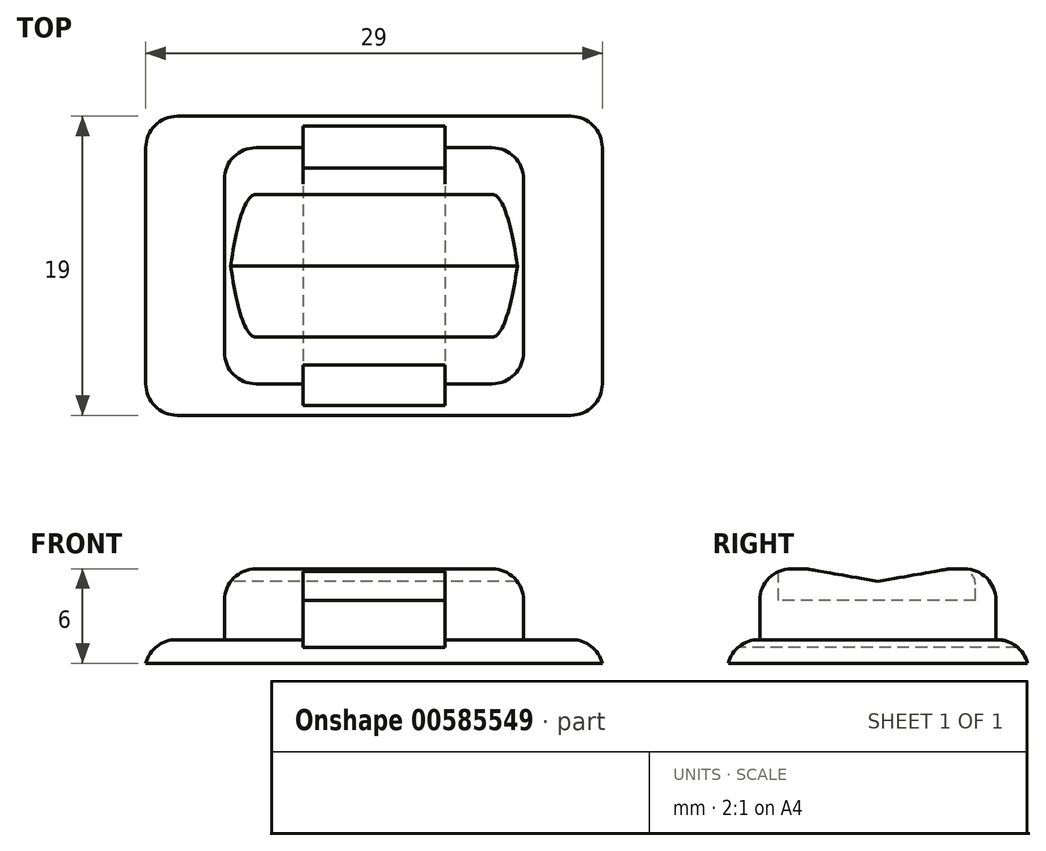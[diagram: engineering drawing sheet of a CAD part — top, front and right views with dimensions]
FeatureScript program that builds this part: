
annotation { "Feature Type Name" : "Feature", "Feature Type Description" : "" }
export const myFeature = defineFeature(function(context is Context, id is Id, definition is map)
    precondition{}
    {
        {
            var Q0;
            Q0=qCreatedBy(makeId("Top.planeOp"),FACE);
            var sketch = newSketch(context, id + "F0", { "sketchPlane" : qUnion([Q0])});
            skLineSegment(sketch, "E0.bottom", {"start": v(-12.5, 9.5) * mm, "end": v(12.5, 9.5) * mm});
            skLineSegment(sketch, "E0.top", {"start": v(-12.5, -9.5) * mm, "end": v(12.5, -9.5) * mm});
            skLineSegment(sketch, "E0.left", {"start": v(-14.5, 7.5) * mm, "end": v(-14.5, -7.5) * mm});
            skLineSegment(sketch, "E0.right", {"start": v(14.5, 7.5) * mm, "end": v(14.5, -7.5) * mm});
            skLineSegment(sketch, "E1", {"start": v(14.5, 9.5) * mm, "end": v(-14.5, -9.5) * mm, "construction": true});
            skLineSegment(sketch, "E2", {"start": v(-14.5, 9.5) * mm, "end": v(14.5, -9.5) * mm, "construction": true});
            skPoint(sketch, "E3.visualSharp", {"position": v(14.5, 9.5) * mm});
            skArc(sketch, "E3.filletArc", {"start": v(14.5, 7.5) * mm, "mid": v(13.91, 8.91) * mm, "end": v(12.5, 9.5) * mm});
            skPoint(sketch, "E4.visualSharp", {"position": v(-14.5, 9.5) * mm});
            skArc(sketch, "E4.filletArc", {"start": v(-12.5, 9.5) * mm, "mid": v(-13.91, 8.91) * mm, "end": v(-14.5, 7.5) * mm});
            skPoint(sketch, "E5.visualSharp", {"position": v(-14.5, -9.5) * mm});
            skArc(sketch, "E5.filletArc", {"start": v(-14.5, -7.5) * mm, "mid": v(-13.91, -8.91) * mm, "end": v(-12.5, -9.5) * mm});
            skPoint(sketch, "E6.visualSharp", {"position": v(14.5, -9.5) * mm});
            skArc(sketch, "E6.filletArc", {"start": v(12.5, -9.5) * mm, "mid": v(13.91, -8.91) * mm, "end": v(14.5, -7.5) * mm});
            skSolve(sketch);
        }
        {
            var Q0;
            Q0 = qSketchRegion(id + "F0", true);
            extrude(context, id + "F1", {"entities" : qUnion([Q0]), "depth" : 1.5 * mm, "offsetDistance" : 25 * mm});
        }
        {
            var Q0;
            Q0=makeQuery(id+"F1.opExtrude","CAP_FACE",FACE,{"disambiguationData":[OSD([sQuery(id+"F0.wireOp",EDGE,"E0.bottom"),sQuery(id+"F0.wireOp",EDGE,"E0.top"),sQuery(id+"F0.wireOp",EDGE,"E0.left"),sQuery(id+"F0.wireOp",EDGE,"E0.right")])],"isStart":false});
            var sketch = newSketch(context, id + "F2", { "sketchPlane" : qUnion([Q0])});
            skLineSegment(sketch, "E7.bottom", {"start": v(-9.5, 7.5) * mm, "end": v(9.5, 7.5) * mm});
            skLineSegment(sketch, "E7.top", {"start": v(-9.5, -7.5) * mm, "end": v(9.5, -7.5) * mm});
            skLineSegment(sketch, "E7.left", {"start": v(-9.5, 7.5) * mm, "end": v(-9.5, -7.5) * mm});
            skLineSegment(sketch, "E7.right", {"start": v(9.5, 7.5) * mm, "end": v(9.5, -7.5) * mm});
            skLineSegment(sketch, "E8", {"start": v(9.5, 7.5) * mm, "end": v(-9.5, -7.5) * mm, "construction": true});
            skLineSegment(sketch, "E9", {"start": v(-9.5, 7.5) * mm, "end": v(9.5, -7.5) * mm, "construction": true});
            skSolve(sketch);
        }
        {
            var Q0;
            Q0 = qSketchRegion(id + "F2", true);
            extrude(context, id + "F3", {"entities" : qUnion([Q0]), "operationType" : NewBodyOperationType.ADD, "depth" : 4.5 * mm, "offsetDistance" : 25 * mm});
        }
        {
            var Q0;
            Q0=qCreatedBy(makeId("Front.planeOp"),FACE);
            var sketch = newSketch(context, id + "F4", { "sketchPlane" : qUnion([Q0])});
            skLineSegment(sketch, "E10.bottom", {"start": v(-4.5, 4) * mm, "end": v(4.5, 4) * mm});
            skLineSegment(sketch, "E10.top", {"start": v(-4.5, 1) * mm, "end": v(4.5, 1) * mm});
            skLineSegment(sketch, "E10.left", {"start": v(-4.5, 4) * mm, "end": v(-4.5, 1) * mm});
            skLineSegment(sketch, "E10.right", {"start": v(4.5, 4) * mm, "end": v(4.5, 1) * mm});
            skLineSegment(sketch, "E11", {"start": v(4.5, 4) * mm, "end": v(-4.5, 1) * mm, "construction": true});
            skLineSegment(sketch, "E12", {"start": v(-4.5, 4) * mm, "end": v(4.5, 1) * mm, "construction": true});
            skPoint(sketch, "E13", {"position": v(0, 2.5) * mm});
            skSolve(sketch);
        }
        {
            var Q0;
            Q0 = qSketchRegion(id + "F4", true);
            extrude(context, id + "F5", {"entities" : qUnion([Q0]), "operationType" : NewBodyOperationType.REMOVE, "endBound" : BoundingType.SYMMETRIC, "oppositeDirection" : true, "depth" : 25 * mm, "offsetDistance" : 25 * mm});
        }
        {
            var Q0;
            Q0=makeQuery(id+"F3.opExtrude","SWEPT_FACE",FACE,{"disambiguationData":[OSD([sQuery(id+"F2.wireOp",EDGE,"E7.top")])]});
            var sketch = newSketch(context, id + "F6", { "sketchPlane" : qUnion([Q0])});
            skLineSegment(sketch, "E14.bottom", {"start": v(-4.5, 4) * mm, "end": v(4.5, 4) * mm});
            skLineSegment(sketch, "E14.top", {"start": v(-4.5, 6) * mm, "end": v(4.5, 6) * mm});
            skLineSegment(sketch, "E14.left", {"start": v(-4.5, 4) * mm, "end": v(-4.5, 6) * mm});
            skLineSegment(sketch, "E14.right", {"start": v(4.5, 4) * mm, "end": v(4.5, 6) * mm});
            skSolve(sketch);
        }
        {
            var Q0;
            Q0 = qSketchRegion(id + "F6", true);
            extrude(context, id + "F7", {"entities" : qUnion([Q0]), "operationType" : NewBodyOperationType.REMOVE, "oppositeDirection" : true, "depth" : 1.2 * mm, "offsetDistance" : 25 * mm});
        }
        {
            var Q0;
            Q0=makeQuery(id+"F3.opExtrude","SWEPT_FACE",FACE,{"disambiguationData":[OSD([sQuery(id+"F2.wireOp",EDGE,"E7.bottom")])]});
            var sketch = newSketch(context, id + "F8", { "sketchPlane" : qUnion([Q0])});
            skLineSegment(sketch, "E15.bottom", {"start": v(-4.5, 4) * mm, "end": v(4.5, 4) * mm});
            skLineSegment(sketch, "E15.top", {"start": v(-4.5, 6) * mm, "end": v(4.5, 6) * mm});
            skLineSegment(sketch, "E15.left", {"start": v(-4.5, 4) * mm, "end": v(-4.5, 6) * mm});
            skLineSegment(sketch, "E15.right", {"start": v(4.5, 4) * mm, "end": v(4.5, 6) * mm});
            skSolve(sketch);
        }
        {
            var Q0;
            Q0 = qSketchRegion(id + "F8", true);
            extrude(context, id + "F9", {"entities" : qUnion([Q0]), "operationType" : NewBodyOperationType.REMOVE, "oppositeDirection" : true, "depth" : 1.3 * mm, "offsetDistance" : 25 * mm});
        }
        {
            var Q0;
            Q0=makeQuery(id+"F3.opExtrude","CAP_EDGE",EDGE,{"disambiguationData":[OSD([sQuery(id+"F2.wireOp",EDGE,"E7.right")])],"isStart":false});
            var Q1;
            Q1=makeQuery(id+"F3.opExtrude","CAP_EDGE",EDGE,{"disambiguationData":[OSD([sQuery(id+"F2.wireOp",EDGE,"E7.left")])],"isStart":false});
            fillet(context, id + "F10", {"entities" : qUnion([Q0, Q1]), "radius" : 2 * mm, "tangentPropagation" : true, "allowEdgeOverflow" : false});
        }
        {
            var Q0;
            {var subQ0=sQuery(id+"F2.wireOp",EDGE,"E7.right");var subQ1=sQuery(id+"F2.wireOp",EDGE,"E7.bottom");Q0=makeQuery(id+"F10.opFillet","BLEND_EDGE",EDGE,{"blendedFrom":[makeQuery(id+"F3.opExtrude","CAP_EDGE",EDGE,{"disambiguationData":[OSD([subQ0])],"isStart":false}),makeQuery(id+"F9.boolean.opBoolean","SPLIT",FACE,{"disambiguationData":[TD([makeQuery(id+"F3.opExtrude","SWEPT_FACE",FACE,{"disambiguationData":[OSD([subQ0])]})])],"derivedFrom":makeQuery(id+"F3.opExtrude","SWEPT_FACE",FACE,{"disambiguationData":[OSD([subQ1])]})})],"blendedInto":[makeQuery(id+"F9.boolean.opBoolean","SPLIT",FACE,{"disambiguationData":[TD([makeQuery(id+"F3.opExtrude","SWEPT_FACE",FACE,{"disambiguationData":[OSD([subQ0])]})])],"derivedFrom":makeQuery(id+"F3.opExtrude","SWEPT_FACE",FACE,{"disambiguationData":[OSD([subQ1])]})})]});}
            var Q1;
            {var subQ0=sQuery(id+"F2.wireOp",EDGE,"E7.right");var subQ1=sQuery(id+"F2.wireOp",EDGE,"E7.bottom");Q1=makeQuery(id+"F9.boolean.opBoolean","SPLIT",EDGE,{"disambiguationData":[TD([makeQuery(id+"F3.opExtrude","SWEPT_FACE",FACE,{"disambiguationData":[OSD([subQ0])]})])],"derivedFrom":makeQuery(id+"F3.opExtrude","CAP_EDGE",EDGE,{"disambiguationData":[OSD([subQ1])],"isStart":false})});}
            var Q2;
            Q2=makeQuery(id+"F3.opExtrude","SWEPT_EDGE",EDGE,{"disambiguationData":[OSD([sQuery(id+"F2.wireOp",EDGE,"E7.bottom"),sQuery(id+"F2.wireOp",EDGE,"E7.right")])]});
            var Q3;
            {var subQ0=sQuery(id+"F2.wireOp",EDGE,"E7.left");var subQ1=sQuery(id+"F2.wireOp",EDGE,"E7.bottom");Q3=makeQuery(id+"F9.boolean.opBoolean","SPLIT",EDGE,{"disambiguationData":[TD([makeQuery(id+"F3.opExtrude","SWEPT_FACE",FACE,{"disambiguationData":[OSD([subQ0])]})])],"derivedFrom":makeQuery(id+"F3.opExtrude","CAP_EDGE",EDGE,{"disambiguationData":[OSD([subQ1])],"isStart":false})});}
            var Q4;
            {var subQ0=sQuery(id+"F2.wireOp",EDGE,"E7.left");var subQ1=sQuery(id+"F2.wireOp",EDGE,"E7.bottom");Q4=makeQuery(id+"F10.opFillet","BLEND_EDGE",EDGE,{"blendedFrom":[makeQuery(id+"F3.opExtrude","CAP_EDGE",EDGE,{"disambiguationData":[OSD([subQ0])],"isStart":false}),makeQuery(id+"F9.boolean.opBoolean","SPLIT",FACE,{"disambiguationData":[TD([makeQuery(id+"F3.opExtrude","SWEPT_FACE",FACE,{"disambiguationData":[OSD([subQ0])]})])],"derivedFrom":makeQuery(id+"F3.opExtrude","SWEPT_FACE",FACE,{"disambiguationData":[OSD([subQ1])]})})],"blendedInto":[makeQuery(id+"F9.boolean.opBoolean","SPLIT",FACE,{"disambiguationData":[TD([makeQuery(id+"F3.opExtrude","SWEPT_FACE",FACE,{"disambiguationData":[OSD([subQ0])]})])],"derivedFrom":makeQuery(id+"F3.opExtrude","SWEPT_FACE",FACE,{"disambiguationData":[OSD([subQ1])]})})]});}
            var Q5;
            Q5=makeQuery(id+"F3.opExtrude","SWEPT_EDGE",EDGE,{"disambiguationData":[OSD([sQuery(id+"F2.wireOp",EDGE,"E7.bottom"),sQuery(id+"F2.wireOp",EDGE,"E7.left")])]});
            var Q6;
            Q6=makeQuery(id+"F3.opExtrude","SWEPT_EDGE",EDGE,{"disambiguationData":[OSD([sQuery(id+"F2.wireOp",EDGE,"E7.top"),sQuery(id+"F2.wireOp",EDGE,"E7.right")])]});
            var Q7;
            {var subQ0=sQuery(id+"F2.wireOp",EDGE,"E7.right");var subQ1=sQuery(id+"F2.wireOp",EDGE,"E7.top");Q7=makeQuery(id+"F10.opFillet","BLEND_EDGE",EDGE,{"blendedFrom":[makeQuery(id+"F3.opExtrude","CAP_EDGE",EDGE,{"disambiguationData":[OSD([subQ0])],"isStart":false}),makeQuery(id+"F7.boolean.opBoolean","SPLIT",FACE,{"disambiguationData":[TD([makeQuery(id+"F3.opExtrude","SWEPT_FACE",FACE,{"disambiguationData":[OSD([subQ0])]})])],"derivedFrom":makeQuery(id+"F3.opExtrude","SWEPT_FACE",FACE,{"disambiguationData":[OSD([subQ1])]})})],"blendedInto":[makeQuery(id+"F7.boolean.opBoolean","SPLIT",FACE,{"disambiguationData":[TD([makeQuery(id+"F3.opExtrude","SWEPT_FACE",FACE,{"disambiguationData":[OSD([subQ0])]})])],"derivedFrom":makeQuery(id+"F3.opExtrude","SWEPT_FACE",FACE,{"disambiguationData":[OSD([subQ1])]})})]});}
            var Q8;
            {var subQ0=sQuery(id+"F2.wireOp",EDGE,"E7.left");var subQ1=sQuery(id+"F2.wireOp",EDGE,"E7.top");Q8=makeQuery(id+"F7.boolean.opBoolean","SPLIT",EDGE,{"disambiguationData":[TD([makeQuery(id+"F3.opExtrude","SWEPT_FACE",FACE,{"disambiguationData":[OSD([subQ0])]})])],"derivedFrom":makeQuery(id+"F3.opExtrude","CAP_EDGE",EDGE,{"disambiguationData":[OSD([subQ1])],"isStart":false})});}
            var Q9;
            {var subQ0=sQuery(id+"F2.wireOp",EDGE,"E7.left");var subQ1=sQuery(id+"F2.wireOp",EDGE,"E7.top");Q9=makeQuery(id+"F10.opFillet","BLEND_EDGE",EDGE,{"blendedFrom":[makeQuery(id+"F3.opExtrude","CAP_EDGE",EDGE,{"disambiguationData":[OSD([subQ0])],"isStart":false}),makeQuery(id+"F7.boolean.opBoolean","SPLIT",FACE,{"disambiguationData":[TD([makeQuery(id+"F3.opExtrude","SWEPT_FACE",FACE,{"disambiguationData":[OSD([subQ0])]})])],"derivedFrom":makeQuery(id+"F3.opExtrude","SWEPT_FACE",FACE,{"disambiguationData":[OSD([subQ1])]})})],"blendedInto":[makeQuery(id+"F7.boolean.opBoolean","SPLIT",FACE,{"disambiguationData":[TD([makeQuery(id+"F3.opExtrude","SWEPT_FACE",FACE,{"disambiguationData":[OSD([subQ0])]})])],"derivedFrom":makeQuery(id+"F3.opExtrude","SWEPT_FACE",FACE,{"disambiguationData":[OSD([subQ1])]})})]});}
            var Q10;
            Q10=makeQuery(id+"F3.opExtrude","SWEPT_EDGE",EDGE,{"disambiguationData":[OSD([sQuery(id+"F2.wireOp",EDGE,"E7.top"),sQuery(id+"F2.wireOp",EDGE,"E7.left")])]});
            var Q11;
            Q11=makeQuery(id+"F1.opExtrude","CAP_EDGE",EDGE,{"disambiguationData":[OSD([sQuery(id+"F0.wireOp",EDGE,"E0.right")])],"isStart":false});
            var Q12;
            Q12=makeQuery(id+"F1.opExtrude","CAP_EDGE",EDGE,{"disambiguationData":[OSD([sQuery(id+"F0.wireOp",EDGE,"E0.left")])],"isStart":false});
            var Q13;
            {var subQ0=sQuery(id+"F0.wireOp",EDGE,"E0.right");var subQ1=sQuery(id+"F0.wireOp",EDGE,"E0.top");Q13=makeQuery(id+"F5.boolean.opBoolean","SPLIT",EDGE,{"disambiguationData":[TD([makeQuery(id+"F1.opExtrude","SWEPT_FACE",FACE,{"disambiguationData":[OSD([subQ0])]})])],"derivedFrom":makeQuery(id+"F1.opExtrude","CAP_EDGE",EDGE,{"disambiguationData":[OSD([subQ1])],"isStart":false})});}
            var Q14;
            {var subQ0=sQuery(id+"F0.wireOp",EDGE,"E0.bottom");var subQ1=sQuery(id+"F0.wireOp",EDGE,"E0.left");Q14=makeQuery(id+"F5.boolean.opBoolean","SPLIT",EDGE,{"disambiguationData":[TD([makeQuery(id+"F1.opExtrude","SWEPT_FACE",FACE,{"disambiguationData":[OSD([subQ1])]})])],"derivedFrom":makeQuery(id+"F1.opExtrude","CAP_EDGE",EDGE,{"disambiguationData":[OSD([subQ0])],"isStart":false})});}
            fillet(context, id + "F11", {"entities" : qUnion([Q0, Q1, Q2, Q3, Q4, Q5, Q6, Q7, Q8, Q9, Q10, Q11, Q12, Q13, Q14]), "radius" : 2 * mm, "tangentPropagation" : true, "allowEdgeOverflow" : false});
        }
        {
            var Q0;
            Q0=makeQuery(id+"F7.boolean.opBoolean","COPY",EDGE,{"derivedFrom":makeQuery(id+"F7.opExtrude","CAP_EDGE",EDGE,{"disambiguationData":[OSD([sQuery(id+"F6.wireOp",EDGE,"E14.bottom")])],"isStart":false})});
            var Q1;
            Q1=makeQuery(id+"F9.boolean.opBoolean","COPY",EDGE,{"derivedFrom":makeQuery(id+"F9.opExtrude","CAP_EDGE",EDGE,{"disambiguationData":[OSD([sQuery(id+"F8.wireOp",EDGE,"E15.bottom")])],"isStart":false})});
            var Q2;
            {var subQ0=sQuery(id+"F8.wireOp",EDGE,"E15.left");var subQ1=sQuery(id+"F2.wireOp",EDGE,"E7.right");var subQ2=sQuery(id+"F2.wireOp",EDGE,"E7.bottom");Q2=makeQuery(id+"F11.opFillet","BLEND_EDGE",EDGE,{"blendedFrom":[makeQuery(id+"F9.boolean.opBoolean","SPLIT",EDGE,{"disambiguationData":[TD([makeQuery(id+"F3.opExtrude","SWEPT_FACE",FACE,{"disambiguationData":[OSD([subQ1])]})])],"derivedFrom":makeQuery(id+"F3.opExtrude","CAP_EDGE",EDGE,{"disambiguationData":[OSD([subQ2])],"isStart":false})}),makeQuery(id+"F9.boolean.opBoolean","COPY",FACE,{"derivedFrom":makeQuery(id+"F9.opExtrude","CAP_FACE",FACE,{"disambiguationData":[OSD([sQuery(id+"F8.wireOp",EDGE,"E15.bottom"),sQuery(id+"F8.wireOp",EDGE,"E15.top"),subQ0,sQuery(id+"F8.wireOp",EDGE,"E15.right")])],"isStart":false})})],"blendedInto":[makeQuery(id+"F9.boolean.opBoolean","COPY",FACE,{"derivedFrom":makeQuery(id+"F9.opExtrude","CAP_FACE",FACE,{"disambiguationData":[OSD([sQuery(id+"F8.wireOp",EDGE,"E15.bottom"),sQuery(id+"F8.wireOp",EDGE,"E15.top"),subQ0,sQuery(id+"F8.wireOp",EDGE,"E15.right")])],"isStart":false})})]});}
            var Q3;
            {var subQ0=sQuery(id+"F6.wireOp",EDGE,"E14.left");var subQ1=sQuery(id+"F2.wireOp",EDGE,"E7.left");var subQ2=sQuery(id+"F2.wireOp",EDGE,"E7.top");Q3=makeQuery(id+"F11.opFillet","BLEND_EDGE",EDGE,{"blendedFrom":[makeQuery(id+"F7.boolean.opBoolean","SPLIT",EDGE,{"disambiguationData":[TD([makeQuery(id+"F3.opExtrude","SWEPT_FACE",FACE,{"disambiguationData":[OSD([subQ1])]})])],"derivedFrom":makeQuery(id+"F3.opExtrude","CAP_EDGE",EDGE,{"disambiguationData":[OSD([subQ2])],"isStart":false})}),makeQuery(id+"F7.boolean.opBoolean","COPY",FACE,{"derivedFrom":makeQuery(id+"F7.opExtrude","CAP_FACE",FACE,{"disambiguationData":[OSD([sQuery(id+"F6.wireOp",EDGE,"E14.bottom"),sQuery(id+"F6.wireOp",EDGE,"E14.top"),subQ0,sQuery(id+"F6.wireOp",EDGE,"E14.right")])],"isStart":false})})],"blendedInto":[makeQuery(id+"F7.boolean.opBoolean","COPY",FACE,{"derivedFrom":makeQuery(id+"F7.opExtrude","CAP_FACE",FACE,{"disambiguationData":[OSD([sQuery(id+"F6.wireOp",EDGE,"E14.bottom"),sQuery(id+"F6.wireOp",EDGE,"E14.top"),subQ0,sQuery(id+"F6.wireOp",EDGE,"E14.right")])],"isStart":false})})]});}
            fillet(context, id + "F12", {"entities" : qUnion([Q0, Q1, Q2, Q3]), "radius" : 1 * mm, "tangentPropagation" : true, "allowEdgeOverflow" : false});
        }
        {
            var Q0;
            Q0=qCreatedBy(makeId("Right.planeOp"),FACE);
            var sketch = newSketch(context, id + "F13", { "sketchPlane" : qUnion([Q0])});
            skLineSegment(sketch, "E16", {"start": v(0, 5.2) * mm, "end": v(10, 6.96) * mm});
            skLineSegment(sketch, "E17", {"start": v(0, 51.34) * mm, "end": v(0, -16.8) * mm, "construction": true});
            skLineSegment(sketch, "E18.MirrorCS", {"start": v(0, 5.2) * mm, "end": v(-10, 6.96) * mm});
            skLineSegment(sketch, "E19.0", {"start": v(-5.5, 6) * mm, "end": v(5.5, 6) * mm, "construction": true});
            skLineSegment(sketch, "E20", {"start": v(10, 6.96) * mm, "end": v(-10, 6.96) * mm});
            skSolve(sketch);
        }
        {
            var Q0;
            Q0 = qSketchRegion(id + "F13", true);
            extrude(context, id + "F14", {"entities" : qUnion([Q0]), "operationType" : NewBodyOperationType.REMOVE, "endBound" : BoundingType.SYMMETRIC, "depth" : 25 * mm, "offsetDistance" : 25 * mm});
        }
    });
